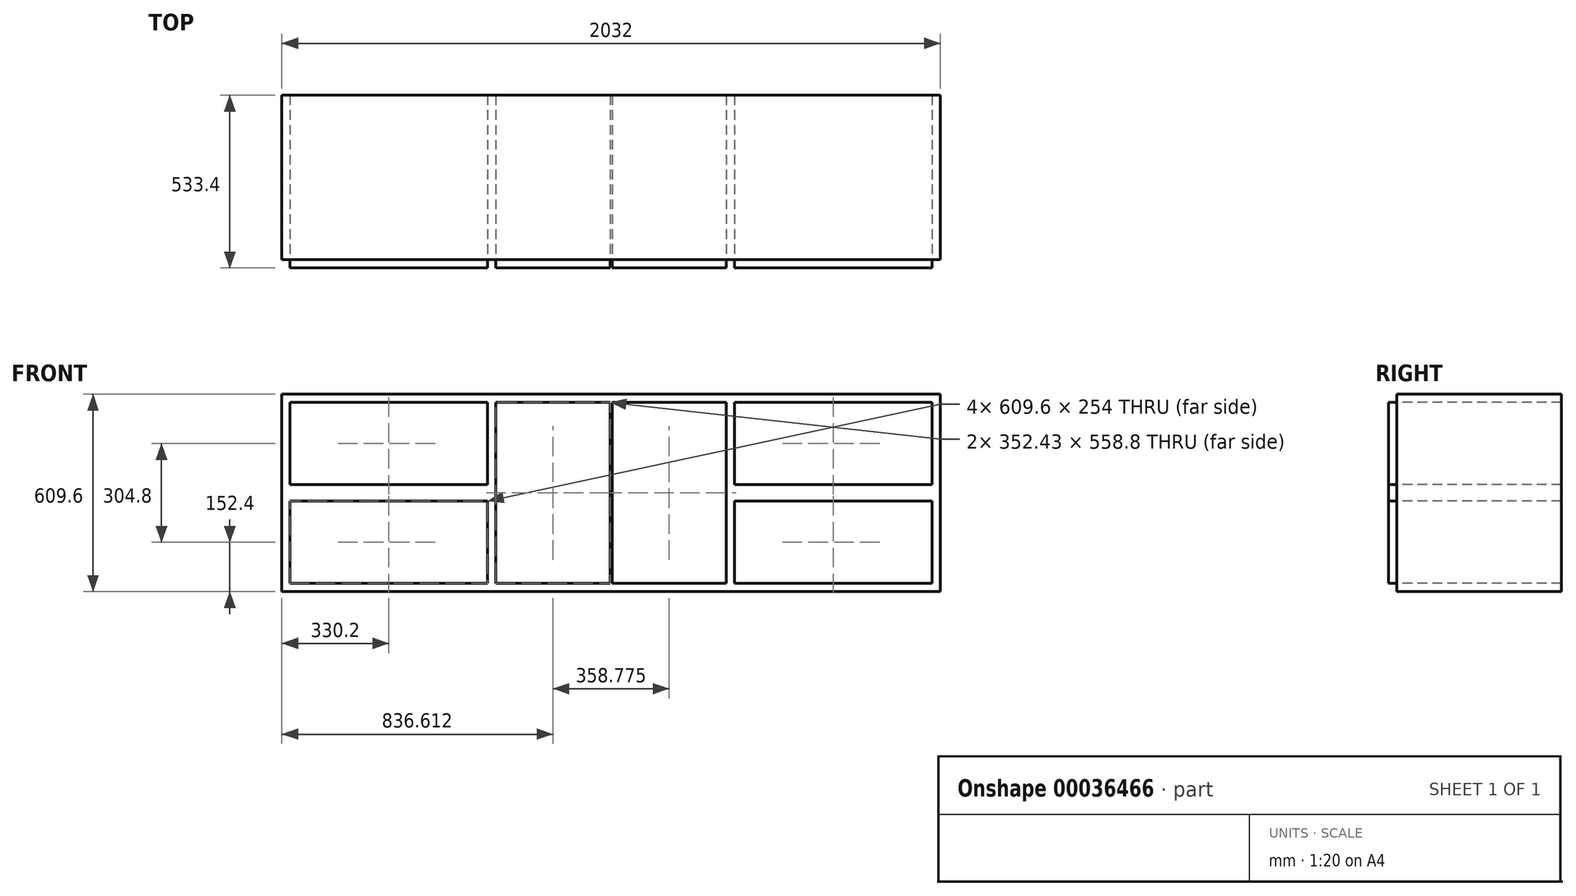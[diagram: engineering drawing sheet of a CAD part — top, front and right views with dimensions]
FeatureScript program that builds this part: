
annotation { "Feature Type Name" : "Feature", "Feature Type Description" : "" }
export const myFeature = defineFeature(function(context is Context, id is Id, definition is map)
    precondition{}
    {
        {
            var Q0;
            Q0=qCreatedBy(makeId("Front.planeOp"),FACE);
            var sketch = newSketch(context, id + "F0", { "sketchPlane" : qUnion([Q0])});
            skLineSegment(sketch, "E0.bottom", {"start": v(-1016, 0) * mm, "end": v(1016, 0) * mm});
            skLineSegment(sketch, "E0.top", {"start": v(-1016, 609.6) * mm, "end": v(1016, 609.6) * mm});
            skLineSegment(sketch, "E0.left", {"start": v(-1016, 0) * mm, "end": v(-1016, 609.6) * mm});
            skLineSegment(sketch, "E0.right", {"start": v(1016, 0) * mm, "end": v(1016, 609.6) * mm});
            skLineSegment(sketch, "E1.bottom", {"start": v(-990.6, 584.2) * mm, "end": v(-381, 584.2) * mm});
            skLineSegment(sketch, "E1.top", {"start": v(-990.6, 330.2) * mm, "end": v(-381, 330.2) * mm});
            skLineSegment(sketch, "E1.left", {"start": v(-990.6, 584.2) * mm, "end": v(-990.6, 330.2) * mm});
            skLineSegment(sketch, "E1.right", {"start": v(-381, 584.2) * mm, "end": v(-381, 330.2) * mm});
            skLineSegment(sketch, "E2.bottom", {"start": v(-990.6, 279.4) * mm, "end": v(-381, 279.4) * mm});
            skLineSegment(sketch, "E2.top", {"start": v(-990.6, 25.4) * mm, "end": v(-381, 25.4) * mm});
            skLineSegment(sketch, "E2.left", {"start": v(-990.6, 279.4) * mm, "end": v(-990.6, 25.4) * mm});
            skLineSegment(sketch, "E2.right", {"start": v(-381, 279.4) * mm, "end": v(-381, 25.4) * mm});
            skLineSegment(sketch, "E3", {"start": v(0, 609.6) * mm, "end": v(0, 0) * mm, "construction": true});
            skLineSegment(sketch, "E4.bottom", {"start": v(-355.6, 584.2) * mm, "end": v(-3.18, 584.2) * mm});
            skLineSegment(sketch, "E4.top", {"start": v(-355.6, 25.4) * mm, "end": v(-3.17, 25.4) * mm});
            skLineSegment(sketch, "E4.left", {"start": v(-355.6, 584.2) * mm, "end": v(-355.6, 25.4) * mm});
            skLineSegment(sketch, "E4.right", {"start": v(-3.18, 584.2) * mm, "end": v(-3.17, 25.4) * mm});
            skLineSegment(sketch, "E5.MirrorCS", {"start": v(990.6, 25.4) * mm, "end": v(381, 25.4) * mm});
            skLineSegment(sketch, "E6.MirrorCS", {"start": v(990.6, 279.4) * mm, "end": v(381, 279.4) * mm});
            skLineSegment(sketch, "E7.MirrorCS", {"start": v(381, 584.2) * mm, "end": v(381, 330.2) * mm});
            skLineSegment(sketch, "E8.MirrorCS", {"start": v(990.6, 584.2) * mm, "end": v(990.6, 330.2) * mm});
            skLineSegment(sketch, "E9.MirrorCS", {"start": v(3.18, 584.2) * mm, "end": v(3.17, 25.4) * mm});
            skLineSegment(sketch, "E10.MirrorCS", {"start": v(990.6, 330.2) * mm, "end": v(381, 330.2) * mm});
            skLineSegment(sketch, "E11.MirrorCS", {"start": v(990.6, 279.4) * mm, "end": v(990.6, 25.4) * mm});
            skLineSegment(sketch, "E12.MirrorCS", {"start": v(355.6, 584.2) * mm, "end": v(355.6, 25.4) * mm});
            skLineSegment(sketch, "E13.MirrorCS", {"start": v(355.6, 25.4) * mm, "end": v(3.17, 25.4) * mm});
            skLineSegment(sketch, "E14.MirrorCS", {"start": v(990.6, 584.2) * mm, "end": v(381, 584.2) * mm});
            skLineSegment(sketch, "E15.MirrorCS", {"start": v(381, 279.4) * mm, "end": v(381, 25.4) * mm});
            skLineSegment(sketch, "E16.MirrorCS", {"start": v(355.6, 584.2) * mm, "end": v(3.18, 584.2) * mm});
            skSolve(sketch);
        }
        {
            var Q0;
            Q0=makeQuery(id+"F0.imprint","IMPRINT",FACE,{"disambiguationData":[TD([[makeQuery(id+"F0.imprint","IMPRINT",EDGE,{"derivedFrom":sQuery(id+"F0.wireOp",EDGE,"E1.bottom")}),-1.0]])]});
            var Q1;
            Q1=makeQuery(id+"F0.imprint","IMPRINT",FACE,{"disambiguationData":[TD([[makeQuery(id+"F0.imprint","IMPRINT",EDGE,{"derivedFrom":sQuery(id+"F0.wireOp",EDGE,"E2.bottom")}),-1.0]])]});
            var Q2;
            Q2=makeQuery(id+"F0.imprint","IMPRINT",FACE,{"disambiguationData":[TD([[makeQuery(id+"F0.imprint","IMPRINT",EDGE,{"derivedFrom":sQuery(id+"F0.wireOp",EDGE,"E7.MirrorCS")}),1.0]])]});
            var Q3;
            Q3=makeQuery(id+"F0.imprint","IMPRINT",FACE,{"disambiguationData":[TD([[makeQuery(id+"F0.imprint","IMPRINT",EDGE,{"derivedFrom":sQuery(id+"F0.wireOp",EDGE,"E5.MirrorCS")}),-1.0]])]});
            var Q4;
            Q4=makeQuery(id+"F0.imprint","IMPRINT",FACE,{"disambiguationData":[TD([[makeQuery(id+"F0.imprint","IMPRINT",EDGE,{"derivedFrom":sQuery(id+"F0.wireOp",EDGE,"E9.MirrorCS")}),1.0]])]});
            var Q5;
            Q5=makeQuery(id+"F0.imprint","IMPRINT",FACE,{"disambiguationData":[TD([[makeQuery(id+"F0.imprint","IMPRINT",EDGE,{"derivedFrom":sQuery(id+"F0.wireOp",EDGE,"E4.bottom")}),-1.0]])]});
            extrude(context, id + "F1", {"entities" : qUnion([Q0, Q1, Q2, Q3, Q4, Q5]), "depth" : 25.4 * mm});
        }
        {
            var Q0;
            Q0=makeQuery(id+"F0.imprint","IMPRINT",FACE,{"disambiguationData":[TD([[makeQuery(id+"F0.imprint","IMPRINT",EDGE,{"derivedFrom":sQuery(id+"F0.wireOp",EDGE,"E0.bottom")}),1.0]])]});
            extrude(context, id + "F2", {"entities" : qUnion([Q0]), "oppositeDirection" : true, "depth" : 508 * mm});
        }
    });
